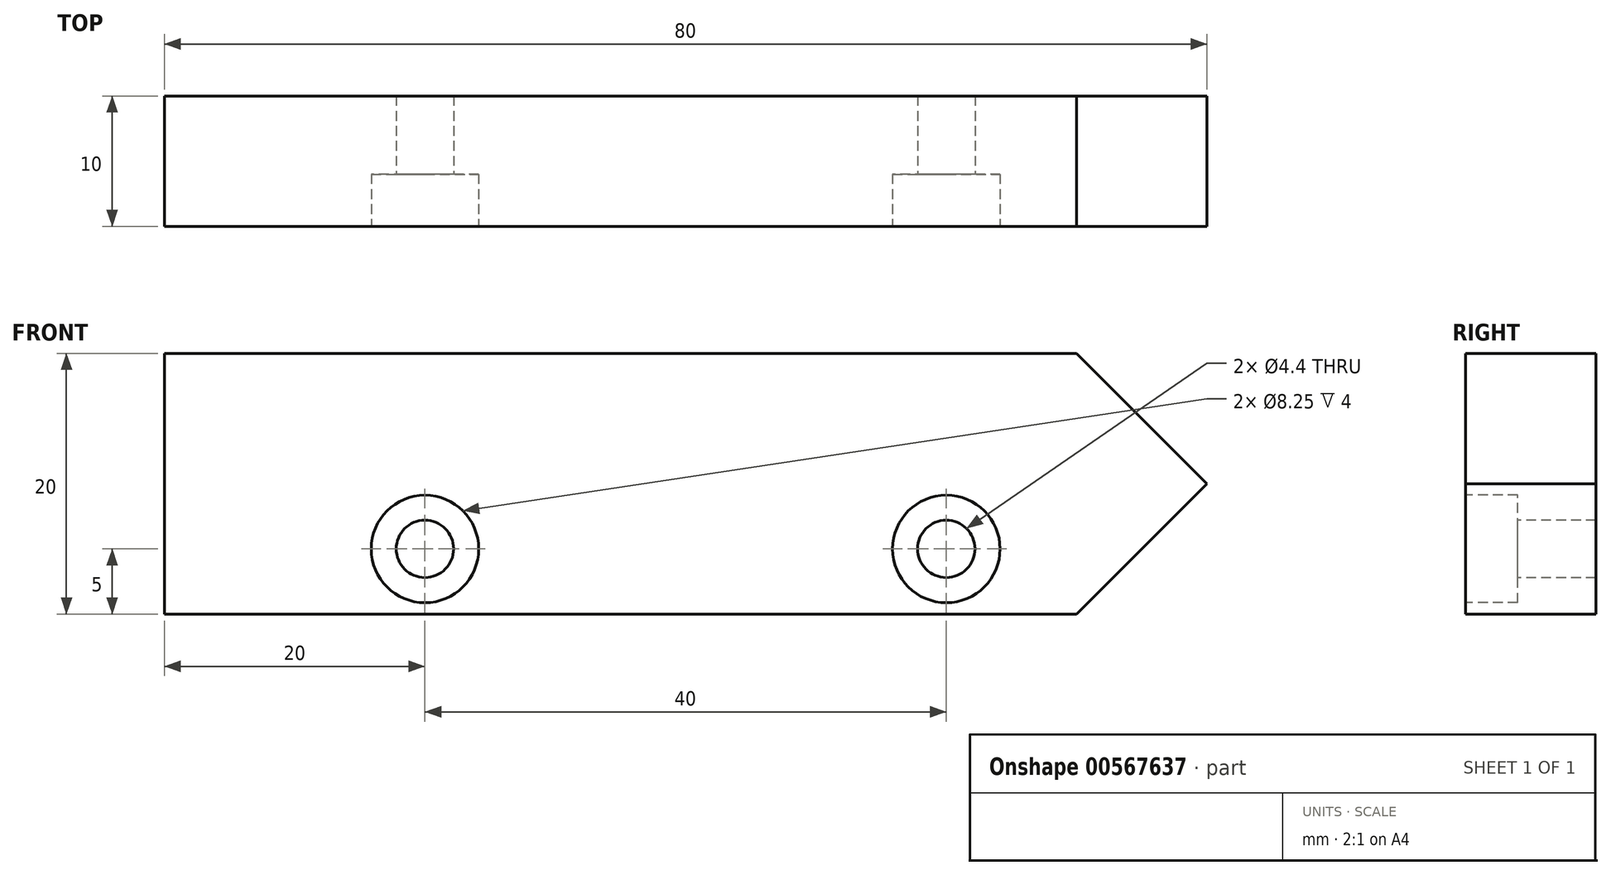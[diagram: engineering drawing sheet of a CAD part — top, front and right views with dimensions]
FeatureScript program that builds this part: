
annotation { "Feature Type Name" : "Feature", "Feature Type Description" : "" }
export const myFeature = defineFeature(function(context is Context, id is Id, definition is map)
    precondition{}
    {
        {
            var Q0;
            Q0=qCreatedBy(makeId("Front.planeOp"),FACE);
            var sketch = newSketch(context, id + "F0", { "sketchPlane" : qUnion([Q0])});
            skLineSegment(sketch, "E0.left", {"start": v(0, 0) * mm, "end": v(0, 20) * mm});
            skLineSegment(sketch, "E1", {"start": v(70, 0) * mm, "end": v(0, 0) * mm});
            skLineSegment(sketch, "E2", {"start": v(0, 10) * mm, "end": v(80, 10) * mm});
            skLineSegment(sketch, "E3", {"start": v(0, 20) * mm, "end": v(70, 20) * mm});
            skLineSegment(sketch, "E4", {"start": v(70, 20) * mm, "end": v(80, 10) * mm});
            skLineSegment(sketch, "E5", {"start": v(70, 0) * mm, "end": v(80, 10) * mm});
            skSolve(sketch);
        }
        {
            var Q0;
            {var subQ2=sQuery(id+"F0.wireOp",EDGE,"XOAGu1b2-GqMS-UDhX-vemc-uYut7se4EIfj");Q0=makeQuery(id+"F0.imprint","IMPRINT",FACE,{"disambiguationData":[TD([[makeQuery(id+"F0.imprint","IMPRINT",EDGE,{"derivedFrom":subQ2}),1.0]])]});}
            var Q1;
            {var subQ0=sQuery(id+"F0.wireOp",EDGE,"E1");Q1=makeQuery(id+"F0.imprint","IMPRINT",FACE,{"disambiguationData":[TD([[makeQuery(id+"F0.imprint","IMPRINT",EDGE,{"derivedFrom":subQ0}),-1.0]])]});}
            var Q2;
            {var subQ2=sQuery(id+"F0.wireOp",EDGE,"E2");Q2=makeQuery(id+"F0.imprint","IMPRINT",FACE,{"disambiguationData":[TD([[makeQuery(id+"F0.imprint","IMPRINT",EDGE,{"derivedFrom":subQ2}),1.0]])]});}
            extrude(context, id + "F1", {"entities" : qUnion([Q0, Q1, Q2]), "depth" : 10 * mm, "offsetDistance" : 25 * mm});
        }
        {
            var Q0;
            Q0=makeQuery(id+"F1.opExtrude","CAP_FACE",FACE,{"disambiguationData":[OSD([sQuery(id+"F0.wireOp",EDGE,"E0.bottom"),sQuery(id+"F0.wireOp",EDGE,"E0.top"),sQuery(id+"F0.wireOp",EDGE,"E0.left"),sQuery(id+"F0.wireOp",EDGE,"E0.right")])],"isStart":false});
            var sketch = newSketch(context, id + "F2", { "sketchPlane" : qUnion([Q0])});
            skLineSegment(sketch, "E6", {"start": v(0, 5) * mm, "end": v(20, 5) * mm});
            skLineSegment(sketch, "E7", {"start": v(60, 0) * mm, "end": v(60, 5) * mm});
            skSolve(sketch);
        }
        {
            var Q0;
            Q0=sQuery(id+"F2.wireOp",VERTEX,"E6.end");
            var Q1;
            Q1=sQuery(id+"F2.wireOp",VERTEX,"E7.end");
            var Q2;
            Q2=makeQuery(id+"F1.opExtrude","SWEPT_BODY",BODY,{"disambiguationData":[OSD([sQuery(id+"F0.wireOp",EDGE,"E0.bottom"),sQuery(id+"F0.wireOp",EDGE,"E0.top"),sQuery(id+"F0.wireOp",EDGE,"E0.left"),sQuery(id+"F0.wireOp",EDGE,"E0.right")])]});
            hole(context, id + "F3", {"style" : HoleStyle.C_BORE, "endStyle" : HoleEndStyle.THROUGH, "standardTappedOrClearance" : lookupTablePath({ "standard" : "ISO", "fit" : "Normal", "size" : "M4", "type" : "Clearance" }), "standardBlindInLast" : lookupTablePath({ "fit" : "Standard", "standard" : "ISO", "size" : "M4", "type" : "Clearance" }), "holeDiameter" : 4.4 * mm, "cBoreDiameter" : 8.25 * mm, "cBoreDepth" : 4 * mm, "isTappedThrough" : true, "tappedDepth" : 12 * mm, "tapClearance" : 3, "locations" : qUnion([Q0, Q1]), "scope" : qUnion([Q2])});
        }
    });
